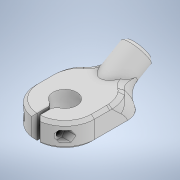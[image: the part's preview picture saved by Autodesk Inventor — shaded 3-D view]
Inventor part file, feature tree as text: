
AUTODESK INVENTOR PART (.ipt)
format: ipt  version: 2021 (Build 250183000, 183)  size: 601,600 bytes
history: native  units: mm
features: extrude x9, sketch x9, chamfer x2, fillet x1
ambient origin geometry x8: Origin, YZ Plane, XZ Plane, XY Plane, X Axis, Y Axis, Z Axis, Center Point
bodies: Solid1 (feature_tree)
feature tree (21):
  extrude  "Extrusion1"  Depth=12.0mm
  extrude  "Extrusion2"  Depth=16.0mm TaperAngle=0.0deg
  extrude  "Extrusion3"  Depth=16.0mm TaperAngle=0.0deg
  extrude  "Extrusion4"  Depth=20.695498mm
  fillet  "Fillet1"  Radius=8.1mm
  chamfer  "Chamfer1"  Distance=25.0mm
  extrude  "Extrusion5"  Depth=2.0mm TaperAngle=45.0deg
  extrude  "Extrusion6"  Depth=2.0mm
  extrude  "Extrusion7"  Depth=10.0mm
  extrude  "Extrusion8"  Depth=10.0mm
  extrude  "Extrusion9"  Depth=10.0mm
  chamfer  "Chamfer2"  Distance=7.0mm
  sketch  "Sketch1"  dims[d0=16.0mm d1=12.0mm]
  sketch  "Sketch3"  dims[d2=16.0mm d3=0.0mm d4=16.0mm d5=0.0mm]
  sketch  "Sketch4"  dims[d6=60.0deg d7=16.0mm d8=0.0mm]
  sketch  "Sketch5"  dims[d9=24.0mm d10=20.695498mm d11=8.1mm]
  sketch  "Sketch6"  dims[d12=9.2375mm]
  sketch  "Sketch7"  dims[d13=20.0mm d14=25.0mm d15=0.0mm]
  sketch  "Sketch8"  dims[d16=12.0mm d17=2.0mm d18=2.0mm d19=45.0deg]
  sketch  "Sketch9"  dims[d20=40.0mm d21=0.0mm d22=2.0mm]
  sketch  "Sketch10"  dims[d23=7.0mm d24=0.0mm d25=4.2mm d26=8.0mm d27=6.0mm d28=7.0mm d29=0.0mm d30=7.2mm d31=10.0mm d32=0.0mm d33=7.1mm d34=10.0mm d35=0.0mm d36=2.0mm d37=2.0mm d38=45.0deg]
